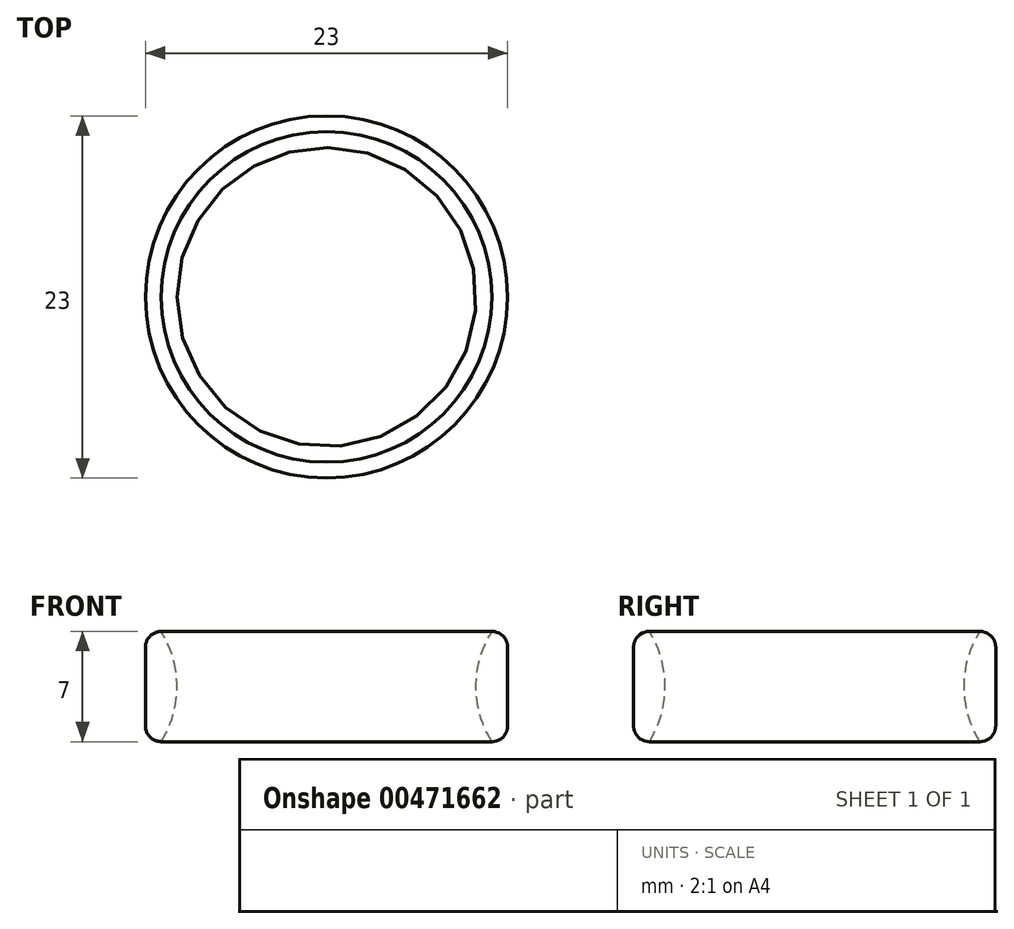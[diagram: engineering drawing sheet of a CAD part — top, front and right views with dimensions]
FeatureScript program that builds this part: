
annotation { "Feature Type Name" : "Feature", "Feature Type Description" : "" }
export const myFeature = defineFeature(function(context is Context, id is Id, definition is map)
    precondition{}
    {
        {
            var Q0;
            Q0=qCreatedBy(makeId("Right.planeOp"),FACE);
            var sketch = newSketch(context, id + "F0", { "sketchPlane" : qUnion([Q0])});
            skLineSegment(sketch, "E0", {"start": v(0, 3.5) * mm, "end": v(0, 0) * mm, "construction": true});
            skLineSegment(sketch, "E1", {"start": v(-1, 0) * mm, "end": v(1, 0) * mm, "construction": true});
            skLineSegment(sketch, "E2", {"start": v(1, 0) * mm, "end": v(1, 2.5) * mm});
            skArc(sketch, "E3", {"start": v(1, 2.5) * mm, "mid": v(0.7, 3.2) * mm, "end": v(0, 3.5) * mm});
            skArc(sketch, "E4", {"start": v(0, 3.5) * mm, "mid": v(-0.75, 1.82) * mm, "end": v(-1, 0) * mm});
            skArc(sketch, "E5.MirrorCS", {"start": v(0, -3.5) * mm, "mid": v(-0.75, -1.82) * mm, "end": v(-1, 0) * mm});
            skArc(sketch, "E6.MirrorCS", {"start": v(1, -2.5) * mm, "mid": v(0.7, -3.2) * mm, "end": v(0, -3.5) * mm});
            skLineSegment(sketch, "E7.MirrorCS", {"start": v(1, 0) * mm, "end": v(1, -2.5) * mm});
            skLineSegment(sketch, "E8", {"start": v(-1, 0) * mm, "end": v(-10.5, 0) * mm, "construction": true});
            skLineSegment(sketch, "E9", {"start": v(-10.5, -5.14) * mm, "end": v(-10.5, 4.36) * mm, "construction": true});
            skSolve(sketch);
        }
        {
            var Q0;
            Q0=makeQuery(id+"F0.imprint","IMPRINT",FACE,{"disambiguationData":[TD([[makeQuery(id+"F0.imprint","IMPRINT",EDGE,{"derivedFrom":sQuery(id+"F0.wireOp",EDGE,"E2")}),1.0]])]});
            var Q1;
            Q1=sQuery(id+"F0.wireOp",EDGE,"E9");
            revolve(context, id + "F1", {"entities" : qUnion([Q0]), "axis" : qUnion([Q1]), "revolveType" : RevolveType.FULL});
        }
    });
